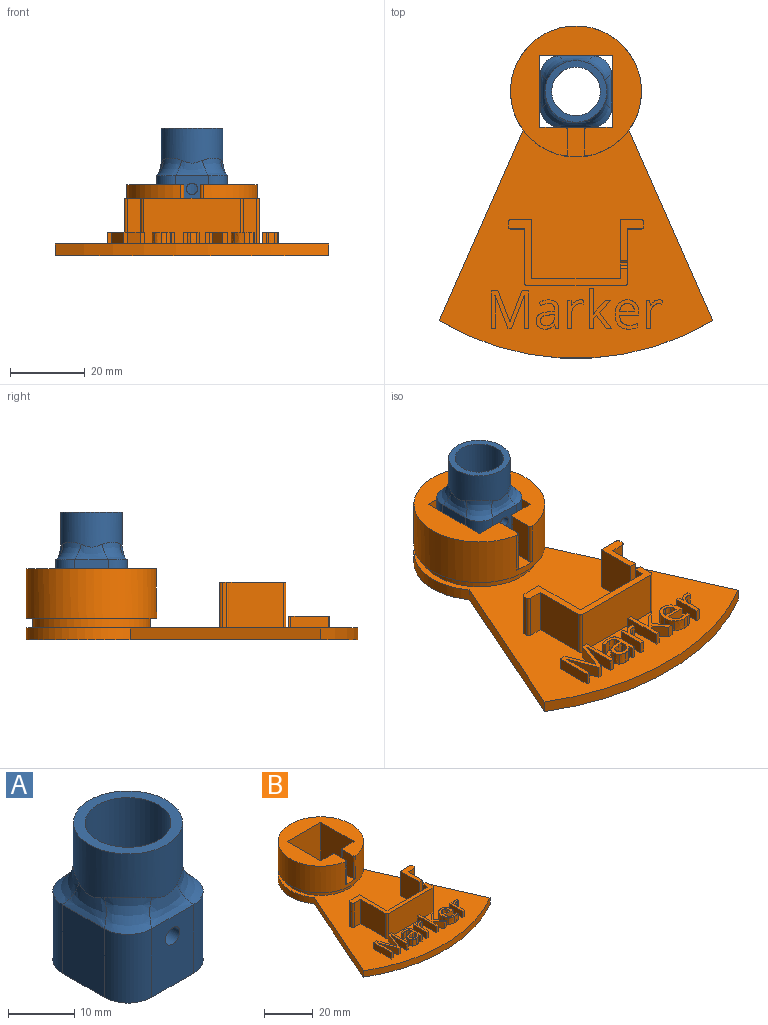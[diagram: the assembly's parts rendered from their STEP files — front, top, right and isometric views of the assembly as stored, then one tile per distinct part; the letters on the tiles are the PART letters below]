
ASSEMBLY  parts=2 mates=1
PART A: 21 faces, bbox 19.2x19.2x25.5 mm
  f0: plane 12.81x9mm, normal (0,1,0), area 112.9mm2, adj f5,f8,f10,f16
  f1: plane 12.81x9mm, normal (-1,0,0), area 112.9mm2, adj f5,f6,f10,f20
  f2: plane 12.81x9mm, normal (0,-1,0), area 105.6mm2, adj f6,f7,f10,f11,f17
  f3: plane 12.81x9mm, normal (1,0,0), area 112.9mm2, adj f7,f8,f10,f13
  f4: plane 16.51x16.51mm, normal (0,0,1), area 81.3mm2, adj f9,f12
  f5: cylinder r=5.08mm len=12.7mm, axis (0,0,1), area 101.3mm2, adj f0,f1,f10,f18
  f6: cylinder r=5.08mm len=12.7mm, axis (0,0,-1), area 101.3mm2, adj f1,f2,f10,f19
  f7: cylinder r=5.08mm len=12.7mm, axis (0,0,1), area 101.3mm2, adj f2,f3,f10,f15
  f8: cylinder r=5.08mm len=12.7mm, axis (0,0,-1), area 101.3mm2, adj f0,f3,f10,f14
  f9: cylinder r=6.5mm len=25.4mm, axis (0,0,-1), area 1030.4mm2, adj f4,f10,f11
  f10: plane 19.05x19.05mm, normal (0,0,-1), area 207.9mm2, adj f0,f1,f2,f3,f5,f6,f7,f8
  f11: cylinder r=1.52mm len=3.05mm, axis (0,-1,0), area 28.9mm2, adj f2,f9
  f12: cylinder r=8.26mm len=16.51mm, axis (0,0,-1), area 445.4mm2, adj f4,f13,f14,f15,f16,f17,f18,f19
  f13: bspline ~10.3x4.28mm, area 29.1mm2, adj f3,f12,f14,f15
  f14: bspline ~7.01x6.95mm, area 40mm2, adj f8,f12,f13,f16
  f15: bspline ~7.01x6.95mm, area 40mm2, adj f7,f12,f13,f17
  f16: bspline ~10.3x4.28mm, area 29.1mm2, adj f0,f12,f14,f18
  f17: bspline ~10.3x4.28mm, area 29.1mm2, adj f2,f12,f15,f19
  f18: bspline ~7.01x6.95mm, area 40mm2, adj f5,f12,f16,f20
  f19: bspline ~7.01x6.95mm, area 40mm2, adj f6,f12,f17,f20
  f20: bspline ~10.3x4.28mm, area 29.1mm2, adj f1,f12,f18,f19
PART B: 169 faces, bbox 73.3x89x19.1 mm
  f0: plane 11x6.35mm, normal (0,0,1), area 32mm2, adj f1,f142,f143,f144,f145,f158,f159,f164
  f1: plane 14.48x12.19mm, normal (1,0,0), area 159.9mm2, adj f0,f4,f142,f147,f155,f164,f165,f166
  f2: cylinder r=17.54mm len=35.07mm, axis (0,0,-1), area 244.9mm2, adj f4,f5,f11,f12
  f3: plane 19.3x19.05mm, normal (0,1,0), area 301mm2, adj f5,f6,f8,f10,f135,f160,f163
  f4: plane 89.04x73.29mm, normal (0,0,1), area 2847.1mm2, adj f1,f2,f11,f12,f13,f18,f19,f20
  f5: plane 89.04x73.29mm, normal (0,0,-1), area 3482.4mm2, adj f2,f3,f6,f7,f8,f11,f12,f13
  f6: plane 19.3x19.05mm, normal (1,0,0), area 367.7mm2, adj f3,f5,f7,f10
  f7: plane 19.3x19.05mm, normal (0,-1,0), area 367.7mm2, adj f5,f6,f8,f10
  f8: plane 19.3x19.05mm, normal (-1,0,0), area 367.7mm2, adj f3,f5,f7,f10
  f9: cylinder r=17.54mm len=35.07mm, axis (0,0,-1), area 1399.1mm2, adj f10,f135,f152,f161,f162
  f10: plane 35.07x34.81mm, normal (0,0,1), area 558.9mm2, adj f3,f6,f7,f8,f9,f133,f134,f160
  f11: plane 51.09x22.46mm, normal (0.92,0.4,0), area 177.2mm2, adj f2,f4,f5,f13
  f12: plane 51.09x22.46mm, normal (-0.92,0.4,0), area 177.2mm2, adj f2,f4,f5,f13
  f13: cylinder r=71.5mm len=73.29mm, axis (0,0,-1), area 244.3mm2, adj f4,f5,f11,f12
  f14: cylinder r=1.59mm len=3.18mm, axis (0,0,-1), area 15.8mm2, adj f5,f15
  f15: plane 3.18x3.18mm, normal (0,0,-1), area 7.9mm2, adj f14
  f16: cylinder r=1.59mm len=3.18mm, axis (0,0,-1), area 15.8mm2, adj f5,f17
  f17: plane 3.18x3.18mm, normal (0,0,-1), area 7.9mm2, adj f16
  f18: plane 8.93x3.42mm, normal (-0.93,-0.36,0), area 30.4mm2, adj f4,f19,f35,f36
  f19: plane 3.18x0.94mm, normal (0,-1,0), area 3mm2, adj f4,f18,f20,f36
  f20: plane 8.92x3.45mm, normal (0.93,-0.36,0), area 30.4mm2, adj f4,f19,f21,f36
  f21: plane 3.18x0.06mm, normal (0,-1,0), area 0.2mm2, adj f4,f20,f22,f36
  f22: extruded ~3.18x2.43mm, area 7.7mm2, adj f4,f21,f23,f36
  f23: plane 6.49x3.18mm, normal (-1,0,0), area 20.6mm2, adj f4,f22,f24,f36
  f24: plane 3.18x1.17mm, normal (0,-1,0), area 3.7mm2, adj f4,f23,f25,f36
  f25: plane 10.07x3.18mm, normal (1,0,0), area 32mm2, adj f4,f24,f26,f36
  f26: plane 3.18x1.75mm, normal (0,1,0), area 5.6mm2, adj f4,f25,f27,f36
  f27: plane 8.31x3.22mm, normal (-0.93,0.36,0), area 28.3mm2, adj f4,f26,f28,f36
  f28: plane 3.18x0.06mm, normal (0,1,0), area 0.2mm2, adj f4,f27,f29,f36
  f29: plane 8.31x3.19mm, normal (0.93,0.36,0), area 28.3mm2, adj f4,f28,f30,f36
  f30: plane 3.18x1.76mm, normal (0,1,0), area 5.6mm2, adj f4,f29,f31,f36
  f31: plane 10.07x3.18mm, normal (-1,0,0), area 32mm2, adj f4,f30,f32,f36
  f32: plane 3.18x1.08mm, normal (0,-1,0), area 3.4mm2, adj f4,f31,f33,f36
  f33: plane 6.41x3.18mm, normal (1,0,0), area 20.3mm2, adj f4,f32,f34,f36
  f34: extruded ~3.18x2.52mm, area 8mm2, adj f4,f33,f35,f36
  f35: plane 3.18x0.06mm, normal (0,-1,0), area 0.2mm2, adj f4,f18,f34,f36
  f36: plane 10.07x9.98mm, normal (0,0,1), area 43.4mm2, adj f18,f19,f20,f21,f22,f23,f24,f25
  f37: extruded ~3.18x1.68mm, area 5.8mm2, adj f38,f63,f64,f65
  f38: extruded ~3.18x1.05mm, area 3.6mm2, adj f37,f39,f64,f65
  f39: extruded ~3.18x0.94mm, area 3.3mm2, adj f38,f40,f64,f65
  f40: extruded ~3.18x1.17mm, area 4.4mm2, adj f39,f41,f64,f65
  f41: extruded ~3.18x1.97mm, area 6.5mm2, adj f40,f42,f64,f65
  f42: plane 3.18x1.14mm, normal (0.04,-1,0), area 3.6mm2, adj f41,f43,f64,f65
  f43: plane 3.18x0.68mm, normal (-1,0,0), area 2.2mm2, adj f42,f63,f64,f65
  f44: plane 3.18x1.08mm, normal (-0.98,-0.21,0), area 3.5mm2, adj f4,f45,f62,f64
  f45: plane 3.18x0.85mm, normal (0,-1,0), area 2.7mm2, adj f4,f44,f46,f64
  f46: plane 5.16x3.18mm, normal (1,0,0), area 16.4mm2, adj f4,f45,f47,f64
  f47: extruded ~3.18x1.92mm, area 6.6mm2, adj f4,f46,f48,f64
  f48: extruded ~3.18x2mm, area 6.8mm2, adj f4,f47,f49,f64
  f49: extruded ~3.18x1.34mm, area 4.3mm2, adj f4,f48,f50,f64
  f50: extruded ~3.18x1.22mm, area 4.2mm2, adj f4,f49,f51,f64
  f51: plane 3.18x0.88mm, normal (-0.93,-0.37,0), area 3mm2, adj f4,f50,f52,f64
  f52: extruded ~3.18x2.13mm, area 7.1mm2, adj f4,f51,f53,f64
  f53: extruded ~3.18x1.22mm, area 4.2mm2, adj f4,f52,f54,f64
  f54: extruded ~3.18x1.31mm, area 4.4mm2, adj f4,f53,f55,f64
  f55: plane 3.18x0.47mm, normal (-1,0,0), area 1.5mm2, adj f4,f54,f56,f64
  f56: plane 3.18x1.28mm, normal (-0.03,1,0), area 4.1mm2, adj f4,f55,f57,f64
  f57: extruded ~3.66x3.18mm, area 15.6mm2, adj f4,f56,f58,f64
  f58: extruded ~3.18x1.65mm, area 5.8mm2, adj f4,f57,f59,f64
  f59: extruded ~3.18x1.76mm, area 6mm2, adj f4,f58,f60,f64
  f60: extruded ~3.18x1.4mm, area 4.6mm2, adj f4,f59,f61,f64
  f61: extruded ~3.18x1.13mm, area 4.7mm2, adj f4,f60,f62,f64
  f62: plane 3.18x0.06mm, normal (0,-1,0), area 0.2mm2, adj f4,f44,f61,f64
  f63: extruded ~3.18x1.64mm, area 5.7mm2, adj f37,f43,f64,f65
  f64: plane 7.81x6.06mm, normal (0,0,1), area 22.3mm2, adj f37,f38,f39,f40,f41,f42,f43,f44
  f65: plane 3.71x2.91mm, normal (0,0,1), area 8.7mm2, adj f37,f38,f39,f40,f41,f42,f43,f63
  f66: extruded ~3.18x0.9mm, area 2.9mm2, adj f4,f67,f78,f79
  f67: extruded ~3.18x1.3mm, area 4.4mm2, adj f4,f66,f68,f79
  f68: extruded ~3.18x1.14mm, area 4.9mm2, adj f4,f67,f69,f79
  f69: plane 3.18x0.06mm, normal (0,1,0), area 0.2mm2, adj f4,f68,f70,f79
  f70: plane 3.18x1.4mm, normal (1,0.09,0), area 4.5mm2, adj f4,f69,f71,f79
  f71: plane 3.18x0.94mm, normal (0,1,0), area 3mm2, adj f4,f70,f72,f79
  f72: plane 7.55x3.18mm, normal (-1,0,0), area 24mm2, adj f4,f71,f73,f79
  f73: plane 3.18x1.14mm, normal (0,-1,0), area 3.6mm2, adj f4,f72,f74,f79
  f74: plane 4.05x3.18mm, normal (1,0,0), area 12.9mm2, adj f4,f73,f75,f79
  f75: extruded ~3.18x1.85mm, area 6.4mm2, adj f4,f74,f76,f79
  f76: extruded ~3.18x1.57mm, area 5.7mm2, adj f4,f75,f77,f79
  f77: extruded ~3.18x0.83mm, area 2.7mm2, adj f4,f76,f78,f79
  f78: plane 3.18x1.06mm, normal (0.99,-0.15,0), area 3.4mm2, adj f4,f66,f77,f79
  f79: plane 7.69x4.35mm, normal (0,0,1), area 11.9mm2, adj f66,f67,f68,f69,f70,f71,f72,f73
  f80: extruded ~3.18x1.1mm, area 4.5mm2, adj f4,f81,f94,f95
  f81: plane 3.18x0.06mm, normal (0,1,0), area 0.2mm2, adj f4,f80,f82,f95
  f82: extruded ~3.18x1.17mm, area 3.7mm2, adj f4,f81,f83,f95
  f83: plane 5.69x3.18mm, normal (1,0,0), area 18.1mm2, adj f4,f82,f84,f95
  f84: plane 3.18x1.13mm, normal (0,1,0), area 3.6mm2, adj f4,f83,f85,f95
  f85: plane 10.72x3.18mm, normal (-1,0,0), area 34mm2, adj f4,f84,f86,f95
  f86: plane 3.18x1.13mm, normal (0,-1,0), area 3.6mm2, adj f4,f85,f87,f95
  f87: plane 3.18x2.82mm, normal (1,0,0), area 9mm2, adj f4,f86,f88,f95
  f88: plane 3.18x0.86mm, normal (0.65,-0.76,0), area 3.6mm2, adj f4,f87,f89,f95
  f89: plane 3.57x3.18mm, normal (-0.8,-0.6,0), area 14.1mm2, adj f4,f88,f90,f95
  f90: plane 3.18x1.38mm, normal (0,-1,0), area 4.4mm2, adj f4,f89,f91,f95
  f91: plane 4.33x3.27mm, normal (0.8,0.6,0), area 17.2mm2, adj f4,f90,f92,f95
  f92: plane 3.22x3.18mm, normal (0.72,-0.69,0), area 14.1mm2, adj f4,f91,f93,f95
  f93: plane 3.18x1.36mm, normal (0,1,0), area 4.3mm2, adj f4,f92,f94,f95
  f94: plane 3.18x2.58mm, normal (-0.73,0.69,0), area 11.3mm2, adj f4,f80,f93,f95
  f95: plane 10.72x6.04mm, normal (0,0,1), area 23mm2, adj f80,f81,f82,f83,f84,f85,f86,f87
  f96: extruded ~3.18x1.45mm, area 5.1mm2, adj f97,f114,f115,f116
  f97: extruded ~3.18x1.38mm, area 4.9mm2, adj f96,f98,f115,f116
  f98: extruded ~3.18x1.66mm, area 5.6mm2, adj f97,f99,f115,f116
  f99: plane 3.95x3.18mm, normal (0,1,0), area 12.5mm2, adj f98,f114,f115,f116
  f100: extruded ~3.18x2.64mm, area 9.3mm2, adj f4,f101,f113,f115
  f101: extruded ~3.18x1.31mm, area 4.2mm2, adj f4,f100,f102,f115
  f102: extruded ~3.18x1.15mm, area 3.8mm2, adj f4,f101,f103,f115
  f103: plane 3.18x1.02mm, normal (1,0,0), area 3.2mm2, adj f4,f102,f104,f115
  f104: extruded ~3.18x2.41mm, area 7.9mm2, adj f4,f103,f105,f115
  f105: extruded ~3.18x1.79mm, area 6.3mm2, adj f4,f104,f106,f115
  f106: extruded ~3.18x2.02mm, area 6.9mm2, adj f4,f105,f107,f115
  f107: plane 5.2x3.18mm, normal (0,-1,0), area 16.5mm2, adj f4,f106,f108,f115
  f108: plane 3.18x0.72mm, normal (1,0,0), area 2.3mm2, adj f4,f107,f109,f115
  f109: extruded ~3.18x2.46mm, area 8.4mm2, adj f4,f108,f110,f115
  f110: extruded ~3.18x2.24mm, area 8mm2, adj f4,f109,f111,f115
  f111: extruded ~3.18x2.42mm, area 8.7mm2, adj f4,f110,f112,f115
  f112: extruded ~3.18x2.9mm, area 9.9mm2, adj f4,f111,f113,f115
  f113: extruded ~3.18x2.83mm, area 9.7mm2, adj f4,f100,f112,f115
  f114: extruded ~3.18x1.64mm, area 5.7mm2, adj f96,f99,f115,f116
  f115: plane 7.83x6.39mm, normal (0,0,1), area 22.7mm2, adj f96,f97,f98,f99,f100,f101,f102,f103
  f116: plane 3.95x2.23mm, normal (0,0,1), area 7.1mm2, adj f96,f97,f98,f99,f114
  f117: extruded ~3.18x0.9mm, area 2.9mm2, adj f4,f118,f129,f130
  f118: extruded ~3.18x1.3mm, area 4.4mm2, adj f4,f117,f119,f130
  f119: extruded ~3.18x1.14mm, area 4.9mm2, adj f4,f118,f120,f130
  f120: plane 3.18x0.06mm, normal (0,1,0), area 0.2mm2, adj f4,f119,f121,f130
  f121: plane 3.18x1.4mm, normal (1,0.09,0), area 4.5mm2, adj f4,f120,f122,f130
  f122: plane 3.18x0.94mm, normal (0,1,0), area 3mm2, adj f4,f121,f123,f130
  f123: plane 7.55x3.18mm, normal (-1,0,0), area 24mm2, adj f4,f122,f124,f130
  f124: plane 3.18x1.14mm, normal (0,-1,0), area 3.6mm2, adj f4,f123,f125,f130
  f125: plane 4.05x3.18mm, normal (1,0,0), area 12.9mm2, adj f4,f124,f126,f130
  f126: extruded ~3.18x1.85mm, area 6.4mm2, adj f4,f125,f127,f130
  f127: extruded ~3.18x1.57mm, area 5.7mm2, adj f4,f126,f128,f130
  f128: extruded ~3.18x0.83mm, area 2.7mm2, adj f4,f127,f129,f130
  f129: plane 3.18x1.06mm, normal (0.99,-0.15,0), area 3.4mm2, adj f4,f117,f128,f130
  f130: plane 7.69x4.35mm, normal (0,0,1), area 11.9mm2, adj f117,f118,f119,f120,f121,f122,f123,f124
  f131: cylinder r=3.97mm len=7.94mm, axis (0,0,-1), area 39.6mm2, adj f5,f132
  f132: plane 7.94x7.94mm, normal (0,0,-1), area 49.5mm2, adj f131
  f133: plane 11.43x6.1mm, normal (1,0,0), area 69.8mm2, adj f10,f135,f160,f161
  f134: plane 11.43x6.1mm, normal (-1,0,0), area 69.8mm2, adj f10,f135,f162,f163
  f135: plane 7.88x6.11mm, normal (0,0,1), area 34.5mm2, adj f3,f9,f133,f134,f160,f161,f162,f163
  f136: plane 15.88x12.19mm, normal (1,0,0), area 193.5mm2, adj f4,f137,f146,f147
  f137: plane 12.19x5.59mm, normal (0,1,0), area 63.1mm2, adj f4,f136,f147,f150,f156
  f138: plane 12.19x1.02mm, normal (-1,0,0), area 12.4mm2, adj f4,f147,f156,f157
  f139: plane 12.19x3.68mm, normal (0,-1,0), area 44.9mm2, adj f4,f140,f147,f157
  f140: plane 14.48x12.19mm, normal (-1,0,0), area 176.5mm2, adj f4,f139,f147,f154
  f141: plane 25.91x12.19mm, normal (0,-1,0), area 315.9mm2, adj f4,f147,f154,f155
  f142: plane 12.19x3.68mm, normal (0,-1,0), area 44.9mm2, adj f0,f1,f4,f158
  f143: plane 12.19x1.02mm, normal (1,0,0), area 12.4mm2, adj f0,f4,f158,f159
  f144: plane 12.19x5.59mm, normal (0,1,0), area 63.1mm2, adj f0,f4,f145,f148,f159
  f145: plane 15.88x12.19mm, normal (-1,0,0), area 176.9mm2, adj f0,f4,f144,f146,f147,f164,f165,f166
  f146: plane 23.62x12.19mm, normal (0,1,0), area 288mm2, adj f4,f136,f145,f147
  f147: plane 31.88x17.78mm, normal (0,0,1), area 98.7mm2, adj f1,f136,f137,f138,f139,f140,f141,f145
  f148: cylinder r=1.27mm len=2.54mm, axis (0,1,0), area 15.2mm2, adj f144,f149
  f149: plane 2.54x2.54mm, normal (0,1,0), area 5.1mm2, adj f148
  f150: cylinder r=1.27mm len=2.54mm, axis (0,1,0), area 15.2mm2, adj f137,f151
  f151: plane 2.54x2.54mm, normal (0,1,0), area 5.1mm2, adj f150
  f152: plane 35.07x35.07mm, normal (0,0,-1), area 178.4mm2, adj f9,f153
  f153: cylinder r=15.83mm len=31.67mm, axis (0,0,-1), area 252.7mm2, adj f4,f152
  f154: cylinder r=0.76mm len=12.19mm, axis (0,0,-1), area 14.6mm2, adj f4,f140,f141,f147
  f155: cylinder r=0.76mm len=12.19mm, axis (0,0,1), area 14.6mm2, adj f1,f4,f141,f147
  f156: cylinder r=0.76mm len=12.19mm, axis (0,0,1), area 14.6mm2, adj f4,f137,f138,f147
  f157: cylinder r=0.76mm len=12.19mm, axis (0,0,1), area 14.6mm2, adj f4,f138,f139,f147
  f158: cylinder r=0.76mm len=12.19mm, axis (0,0,1), area 14.6mm2, adj f0,f4,f142,f143
  f159: cylinder r=0.76mm len=12.19mm, axis (0,0,-1), area 14.6mm2, adj f0,f4,f143,f144
  f160: cylinder r=0.76mm len=11.43mm, axis (0,0,-1), area 13.7mm2, adj f3,f10,f133,f135
  f161: cylinder r=0.76mm len=11.43mm, axis (0,0,-1), area 15.2mm2, adj f9,f10,f133,f135
  f162: cylinder r=0.76mm len=11.43mm, axis (0,0,-1), area 15.2mm2, adj f9,f10,f134,f135
  f163: cylinder r=0.76mm len=11.43mm, axis (0,0,1), area 13.7mm2, adj f3,f10,f134,f135
  f164: plane 7.62x1.91mm, normal (0,-1,0), area 14.5mm2, adj f0,f1,f145,f168
  f165: plane 7.62x1.91mm, normal (0,1,0), area 14.5mm2, adj f1,f145,f147,f167
  f166: plane 1.91x0.76mm, normal (0,0,1), area 1.5mm2, adj f1,f145,f167,f168
  f167: cylinder r=0.64mm len=1.91mm, axis (1,0,0), area 1.9mm2, adj f1,f145,f165,f166
  f168: cylinder r=0.64mm len=1.91mm, axis (-1,0,0), area 1.9mm2, adj f1,f145,f164,f166
PLACE A t=(0,0,-10.26)mm
PLACE B t=(0,0,-19.05)mm
MATE slider A.f9 <-> B.f2  axis (0,0,1) through (0,0,15.14)mm
